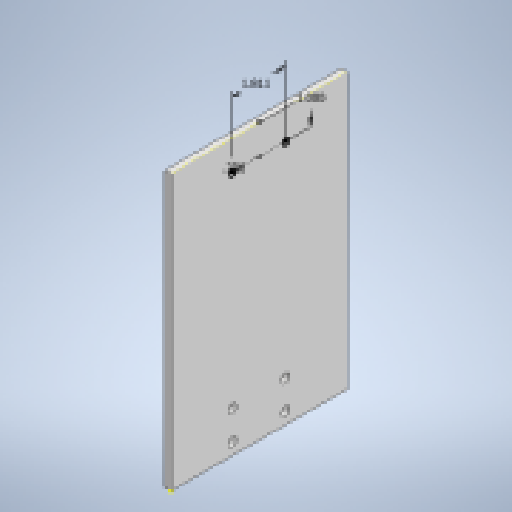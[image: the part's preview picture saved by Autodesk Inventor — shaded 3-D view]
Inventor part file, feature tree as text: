
AUTODESK INVENTOR PART (.ipt)
format: ipt  version: 2023 (Build 270158000, 158)  size: 153,600 bytes
history: native  units: in
note: dims shown in document units (in); Inventor stores cm internally (conversion verified against a paired STEP export)
features: extrude x3, sketch x3
ambient origin geometry x8: Origin, YZ Plane, XZ Plane, XY Plane, X Axis, Y Axis, Z Axis, Center Point
bodies: Solid1 (feature_tree)
feature tree (6):
  extrude  "Extrusion1"  Depth=9.3622in
  extrude  "Extrusion2"  Depth=0.2in
  extrude  "Extrusion3"  Depth=0.2in
  sketch  "Sketch1"  dims[d0=6.0in d1=9.3622in]
  sketch  "Sketch2"  dims[d2=0.2in d3=0.0in d4=0.315in]
  sketch  "Sketch3"  dims[d5=1.811in d6=0.9843in d7=0.3937in d8=0.2in d9=0.0in d10=0.2362in d11=1.0in d12=1.811in d13=0.2in d14=0.0in]
